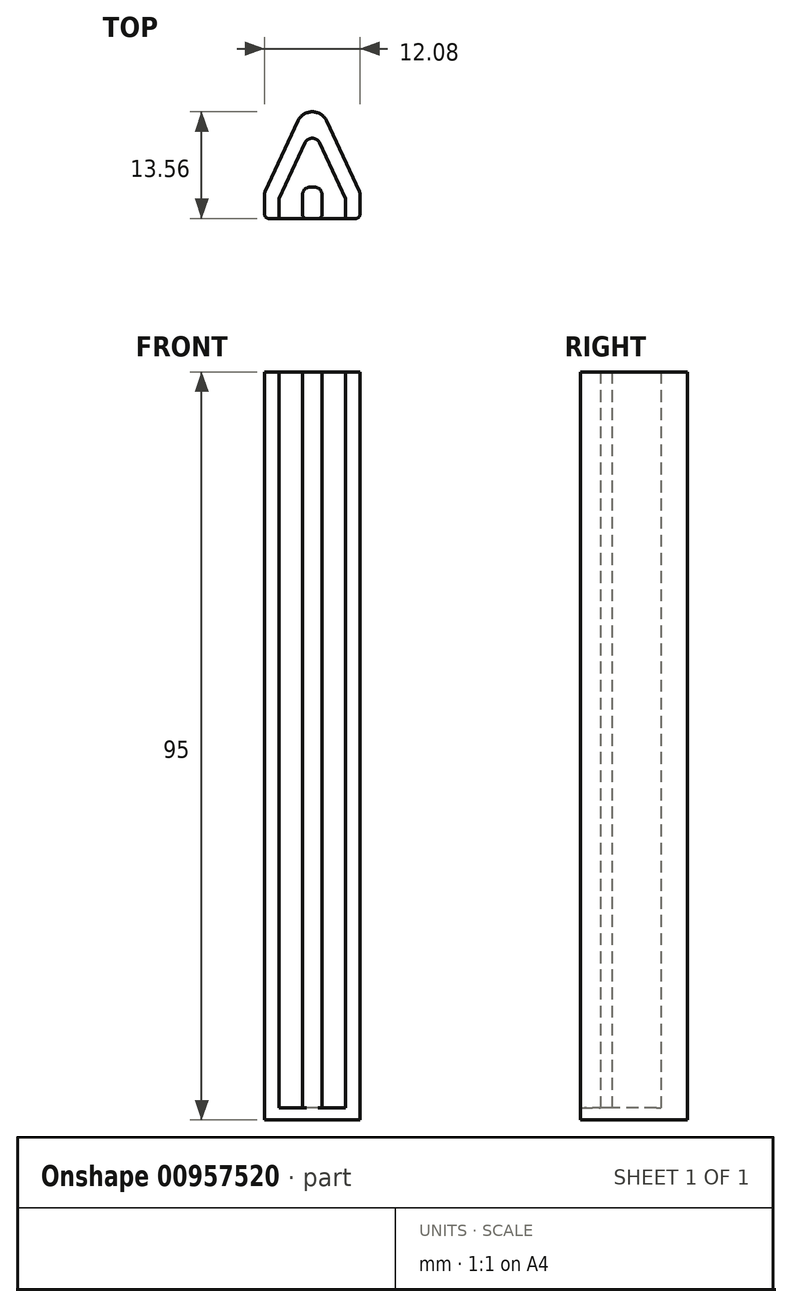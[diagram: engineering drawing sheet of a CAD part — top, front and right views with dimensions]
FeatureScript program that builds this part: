
annotation { "Feature Type Name" : "Feature", "Feature Type Description" : "" }
export const myFeature = defineFeature(function(context is Context, id is Id, definition is map)
    precondition{}
    {
        {
            var Q0;
            Q0=qCreatedBy(makeId("Top.planeOp"),FACE);
            var sketch = newSketch(context, id + "F0", { "sketchPlane" : qUnion([Q0])});
            skLineSegment(sketch, "E0", {"start": v(-0.9, -1.94) * mm, "end": v(-4.23, -9.06) * mm});
            skLineSegment(sketch, "E1", {"start": v(4.23, -9.06) * mm, "end": v(0.9, -1.94) * mm});
            skLineSegment(sketch, "E2.0", {"start": v(-1.81, 0.85) * mm, "end": v(-6.04, -8.22) * mm});
            skLineSegment(sketch, "E2.1", {"start": v(6.04, -8.22) * mm, "end": v(1.81, 0.85) * mm});
            skPoint(sketch, "E3.visualSharp", {"position": v(0, 4.73) * mm});
            skArc(sketch, "E3.filletArc", {"start": v(1.81, 0.85) * mm, "mid": v(0, 2) * mm, "end": v(-1.81, 0.85) * mm});
            skArc(sketch, "E4.filletArc", {"start": v(0.9, -1.94) * mm, "mid": v(0, -1.37) * mm, "end": v(-0.9, -1.94) * mm});
            skLineSegment(sketch, "E5", {"start": v(-4.23, -9.06) * mm, "end": v(-4.23, -11.56) * mm});
            skLineSegment(sketch, "E6", {"start": v(4.23, -9.06) * mm, "end": v(4.23, -11.56) * mm});
            skLineSegment(sketch, "E7", {"start": v(-6.04, -8.22) * mm, "end": v(-6.04, -11.56) * mm});
            skLineSegment(sketch, "E8", {"start": v(-6.04, -11.56) * mm, "end": v(-4.23, -11.56) * mm});
            skLineSegment(sketch, "E9", {"start": v(6.04, -8.22) * mm, "end": v(6.04, -11.56) * mm});
            skLineSegment(sketch, "E10", {"start": v(6.04, -11.56) * mm, "end": v(4.23, -11.56) * mm});
            skLineSegment(sketch, "E11", {"start": v(-1.25, -11.56) * mm, "end": v(-1.25, -8.56) * mm});
            skLineSegment(sketch, "E12", {"start": v(-0.25, -7.56) * mm, "end": v(0.25, -7.56) * mm});
            skLineSegment(sketch, "E13", {"start": v(1.25, -8.56) * mm, "end": v(1.25, -11.56) * mm});
            skPoint(sketch, "E14.visualSharp", {"position": v(-1.25, -7.56) * mm});
            skArc(sketch, "E14.filletArc", {"start": v(-0.25, -7.56) * mm, "mid": v(-0.96, -7.86) * mm, "end": v(-1.25, -8.56) * mm});
            skPoint(sketch, "E15.visualSharp", {"position": v(1.25, -7.56) * mm});
            skArc(sketch, "E15.filletArc", {"start": v(1.25, -8.56) * mm, "mid": v(0.96, -7.86) * mm, "end": v(0.25, -7.56) * mm});
            skLineSegment(sketch, "E16", {"start": v(0, -2.37) * mm, "end": v(0, -11.56) * mm, "construction": true});
            skLineSegment(sketch, "E17", {"start": v(0, -7.56) * mm, "end": v(0, -11.56) * mm, "construction": true});
            skLineSegment(sketch, "E18", {"start": v(4.23, -11.56) * mm, "end": v(-4.23, -11.56) * mm});
            skSolve(sketch);
        }
        {
            var Q0;
            Q0=makeQuery(id+"F0.imprint","IMPRINT",FACE,{"disambiguationData":[TD([[makeQuery(id+"F0.imprint","IMPRINT",EDGE,{"derivedFrom":sQuery(id+"F0.wireOp",EDGE,"E0")}),1.0]])]});
            var Q1;
            Q1=makeQuery(id+"F0.imprint","IMPRINT",FACE,{"disambiguationData":[TD([[makeQuery(id+"F0.imprint","IMPRINT",EDGE,{"derivedFrom":sQuery(id+"F0.wireOp",EDGE,"E0")}),-1.0]])]});
            var Q2;
            Q2=makeQuery(id+"F0.imprint","IMPRINT",FACE,{"disambiguationData":[TD([[makeQuery(id+"F0.imprint","IMPRINT",EDGE,{"derivedFrom":sQuery(id+"F0.wireOp",EDGE,"ALs71zWu-VNMW-JlBQ-uVYK-AxBfpGX4I2zq")}),1.0]])]});
            var Q3;
            {var subQ1=sQuery(id+"F0.wireOp",EDGE,"E11");Q3=makeQuery(id+"F0.imprint","IMPRINT",FACE,{"disambiguationData":[TD([[makeQuery(id+"F0.imprint","IMPRINT",EDGE,{"derivedFrom":subQ1}),-1.0]])]});}
            extrude(context, id + "F1", {"entities" : qUnion([Q0, Q1, Q2, Q3]), "depth" : 1.5 * mm, "offsetDistance" : 25 * mm});
        }
        {
            var Q0;
            Q0=makeQuery(id+"F0.imprint","IMPRINT",FACE,{"disambiguationData":[TD([[makeQuery(id+"F0.imprint","IMPRINT",EDGE,{"derivedFrom":sQuery(id+"F0.wireOp",EDGE,"E0")}),-1.0]])]});
            var Q1;
            {var subQ1=sQuery(id+"F0.wireOp",EDGE,"E11");Q1=makeQuery(id+"F0.imprint","IMPRINT",FACE,{"disambiguationData":[TD([[makeQuery(id+"F0.imprint","IMPRINT",EDGE,{"derivedFrom":subQ1}),-1.0]])]});}
            extrude(context, id + "F2", {"entities" : qUnion([Q0, Q1]), "operationType" : NewBodyOperationType.ADD, "depth" : 95 * mm, "offsetDistance" : 25 * mm});
        }
        {
            var Q0;
            {var subQ0=sQuery(id+"F0.wireOp",EDGE,"E7");var subQ1=sQuery(id+"F0.wireOp",EDGE,"E2.0");Q0=makeQuery(id+"F2.boolean.opBoolean","MERGE",EDGE,{"derivedFrom":[makeQuery(id+"F1.opExtrude","SWEPT_EDGE",EDGE,{"disambiguationData":[OSD([subQ1,subQ0])]}),makeQuery(id+"F2.opExtrude","SWEPT_EDGE",EDGE,{"disambiguationData":[OSD([subQ1,subQ0])]})]});}
            var Q1;
            {var subQ0=sQuery(id+"F0.wireOp",EDGE,"E8");var subQ1=sQuery(id+"F0.wireOp",EDGE,"E7");Q1=makeQuery(id+"F2.boolean.opBoolean","MERGE",EDGE,{"derivedFrom":[makeQuery(id+"F1.opExtrude","SWEPT_EDGE",EDGE,{"disambiguationData":[OSD([subQ1,subQ0])]}),makeQuery(id+"F2.opExtrude","SWEPT_EDGE",EDGE,{"disambiguationData":[OSD([subQ1,subQ0])]})]});}
            var Q2;
            {var subQ0=sQuery(id+"F0.wireOp",EDGE,"E9");var subQ1=sQuery(id+"F0.wireOp",EDGE,"E2.1");Q2=makeQuery(id+"F2.boolean.opBoolean","MERGE",EDGE,{"derivedFrom":[makeQuery(id+"F1.opExtrude","SWEPT_EDGE",EDGE,{"disambiguationData":[OSD([subQ1,subQ0])]}),makeQuery(id+"F2.opExtrude","SWEPT_EDGE",EDGE,{"disambiguationData":[OSD([subQ1,subQ0])]})]});}
            var Q3;
            {var subQ0=sQuery(id+"F0.wireOp",EDGE,"E10");var subQ1=sQuery(id+"F0.wireOp",EDGE,"E9");Q3=makeQuery(id+"F2.boolean.opBoolean","MERGE",EDGE,{"derivedFrom":[makeQuery(id+"F1.opExtrude","SWEPT_EDGE",EDGE,{"disambiguationData":[OSD([subQ1,subQ0])]}),makeQuery(id+"F2.opExtrude","SWEPT_EDGE",EDGE,{"disambiguationData":[OSD([subQ1,subQ0])]})]});}
            var Q4;
            Q4=makeQuery(id+"F2.opExtrude","SWEPT_EDGE",EDGE,{"disambiguationData":[OSD([sQuery(id+"F0.wireOp",EDGE,"E11"),sQuery(id+"F0.wireOp",EDGE,"E18")])]});
            var Q5;
            Q5=makeQuery(id+"F2.opExtrude","SWEPT_EDGE",EDGE,{"disambiguationData":[OSD([sQuery(id+"F0.wireOp",EDGE,"E13"),sQuery(id+"F0.wireOp",EDGE,"E18")])]});
            fillet(context, id + "F3", {"entities" : qUnion([Q0, Q1, Q2, Q3, Q4, Q5]), "radius" : .5 * mm, "tangentPropagation" : true, "allowEdgeOverflow" : false});
        }
    });
